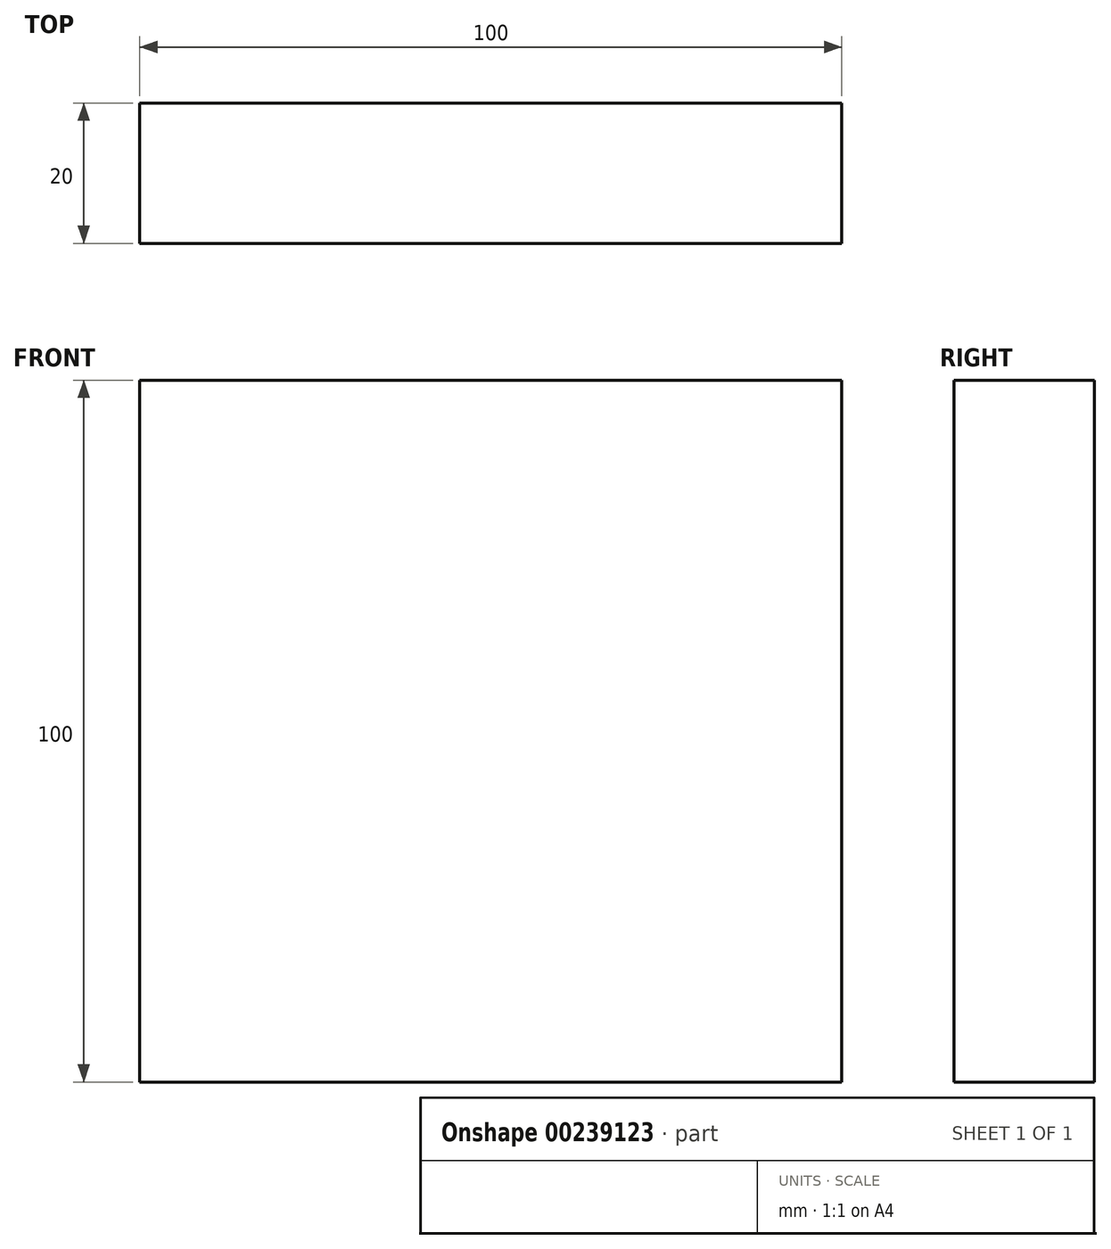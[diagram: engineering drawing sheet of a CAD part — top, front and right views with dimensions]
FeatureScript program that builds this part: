
annotation { "Feature Type Name" : "Feature", "Feature Type Description" : "" }
export const myFeature = defineFeature(function(context is Context, id is Id, definition is map)
    precondition{}
    {
        {
            assignVariable(context, id + "F0", {"name" : "v", "anyValue" : 10});
        }
        {
            var Q0;
            Q0=qCreatedBy(makeId("Front.planeOp"),FACE);
            var sketch = newSketch(context, id + "F1", { "sketchPlane" : qUnion([Q0])});
            skLineSegment(sketch, "E0.bottom", {"start": v(50, 50) * mm, "end": v(-50, 50) * mm});
            skLineSegment(sketch, "E0.top", {"start": v(50, -50) * mm, "end": v(-50, -50) * mm});
            skLineSegment(sketch, "E0.left", {"start": v(50, 50) * mm, "end": v(50, -50) * mm});
            skLineSegment(sketch, "E0.right", {"start": v(-50, 50) * mm, "end": v(-50, -50) * mm});
            skPoint(sketch, "E0.middle", {"position": v(0, 0) * mm});
            skSolve(sketch);
        }
        {
            var Q0;
            Q0 = qSketchRegion(id + "F1", true);
            extrude(context, id + "F2", {"entities" : qUnion([Q0]), "endBound" : BoundingType.SYMMETRIC, "depth" : (2 * getVariable(context, 'v')) * mm});
        }
    });
